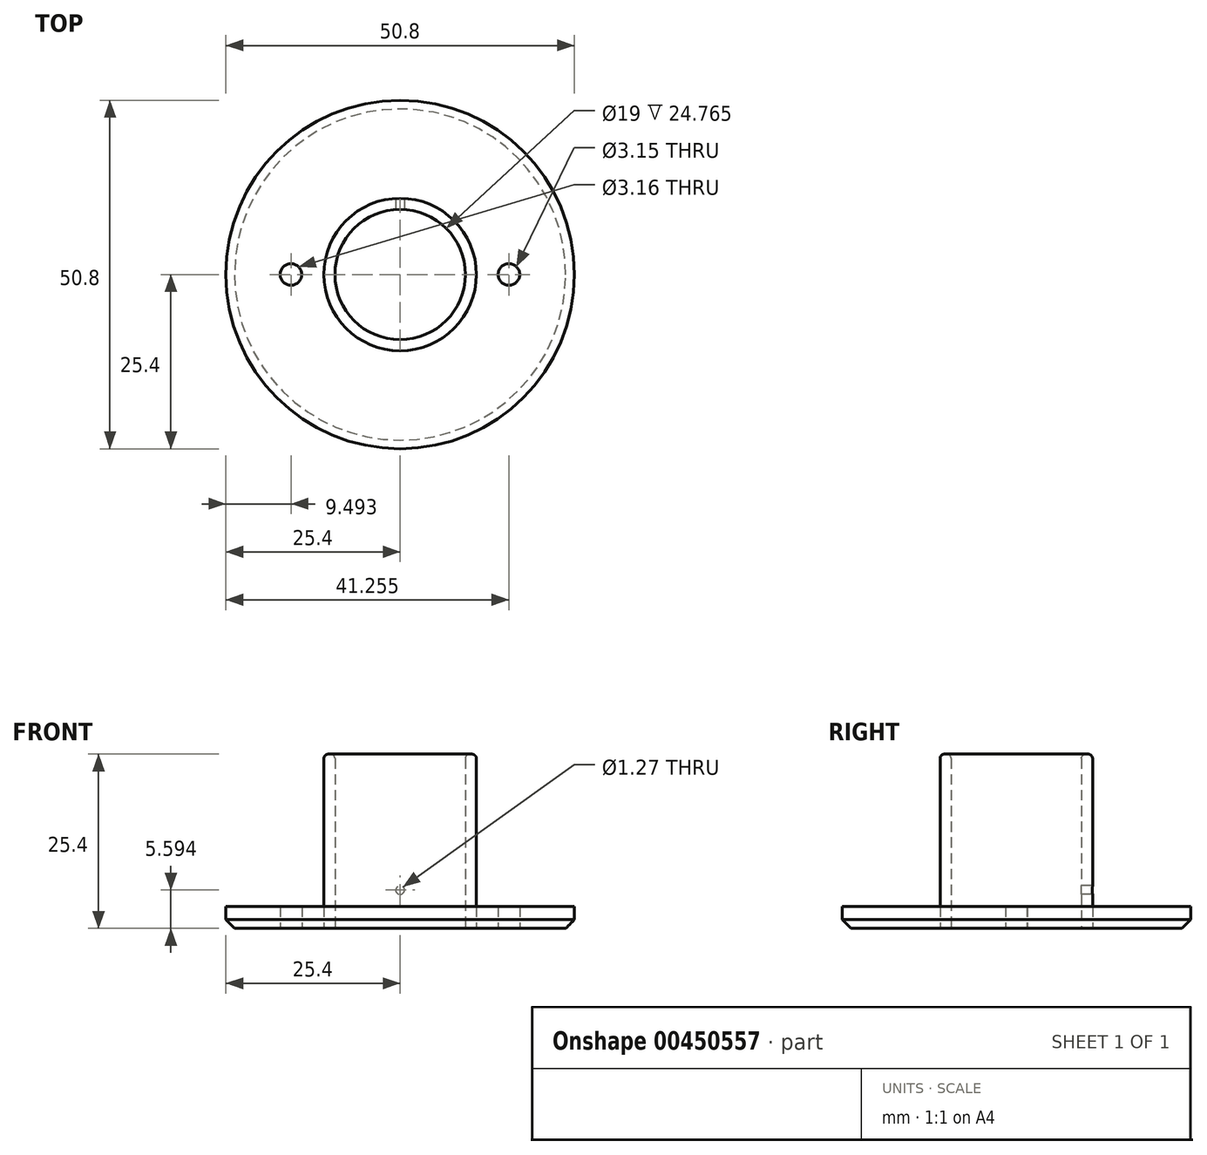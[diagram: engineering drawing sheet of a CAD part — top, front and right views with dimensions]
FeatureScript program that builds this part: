
annotation { "Feature Type Name" : "Feature", "Feature Type Description" : "" }
export const myFeature = defineFeature(function(context is Context, id is Id, definition is map)
    precondition{}
    {
        {
            var Q0;
            Q0=qCreatedBy(makeId("Top.planeOp"),FACE);
            var sketch = newSketch(context, id + "F0", { "sketchPlane" : qUnion([Q0])});
            skCircle(sketch, "E0", {"center": v(0, 0) * mm, "radius": 25.4 * mm});
            skCircle(sketch, "E1", {"center": v(0, 0) * mm, "radius": 9.5 * mm});
            skCircle(sketch, "E2", {"center": v(0, 0) * mm, "radius": 11.1 * mm});
            skLineSegment(sketch, "E3", {"start": v(0, 0) * mm, "end": v(15.86, 0) * mm});
            skLineSegment(sketch, "E4", {"start": v(0, 0) * mm, "end": v(-15.9, 0) * mm});
            skCircle(sketch, "E5", {"center": v(-15.9, 0) * mm, "radius": 1.58 * mm});
            skCircle(sketch, "E6", {"center": v(15.86, 0) * mm, "radius": 1.58 * mm});
            skSolve(sketch);
        }
        {
            var Q0;
            {var subQ0=sQuery(id+"F0.wireOp",EDGE,"E3");var subQ1=sQuery(id+"F0.wireOp",EDGE,"E1");var subQ2=makeQuery(id+"F0.imprint","INTERSECT",VERTEX,{"derivedFrom":[subQ1,subQ0]});Q0=makeQuery(id+"F0.imprint","IMPRINT",FACE,{"disambiguationData":[TD([[makeQuery(id+"F0.imprint","IMPRINT",EDGE,{"disambiguationData":[TD([[subQ2,-1.0]])],"derivedFrom":subQ1}),1.0]])]});}
            var Q1;
            {var subQ0=sQuery(id+"F0.wireOp",EDGE,"E3");var subQ1=sQuery(id+"F0.wireOp",EDGE,"E1");var subQ2=makeQuery(id+"F0.imprint","INTERSECT",VERTEX,{"derivedFrom":[subQ1,subQ0]});Q1=makeQuery(id+"F0.imprint","IMPRINT",FACE,{"disambiguationData":[TD([[makeQuery(id+"F0.imprint","IMPRINT",EDGE,{"disambiguationData":[TD([[subQ2,1.0]])],"derivedFrom":subQ1}),1.0]])]});}
            var Q2;
            {var subQ0=sQuery(id+"F0.wireOp",EDGE,"E3");var subQ1=sQuery(id+"F0.wireOp",EDGE,"E1");var subQ2=makeQuery(id+"F0.imprint","INTERSECT",VERTEX,{"derivedFrom":[subQ1,subQ0]});Q2=makeQuery(id+"F0.imprint","IMPRINT",FACE,{"disambiguationData":[TD([[makeQuery(id+"F0.imprint","IMPRINT",EDGE,{"disambiguationData":[TD([[subQ2,-1.0]])],"derivedFrom":subQ1}),-1.0]])]});}
            var Q3;
            {var subQ0=sQuery(id+"F0.wireOp",EDGE,"E3");var subQ1=sQuery(id+"F0.wireOp",EDGE,"E1");var subQ2=makeQuery(id+"F0.imprint","INTERSECT",VERTEX,{"derivedFrom":[subQ1,subQ0]});Q3=makeQuery(id+"F0.imprint","IMPRINT",FACE,{"disambiguationData":[TD([[makeQuery(id+"F0.imprint","IMPRINT",EDGE,{"disambiguationData":[TD([[subQ2,1.0]])],"derivedFrom":subQ1}),-1.0]])]});}
            var Q4;
            Q4=makeQuery(id+"F0.imprint","IMPRINT",FACE,{"disambiguationData":[TD([[makeQuery(id+"F0.imprint","IMPRINT",EDGE,{"derivedFrom":sQuery(id+"F0.wireOp",EDGE,"E0")}),1.0]])]});
            extrude(context, id + "F1", {"entities" : qUnion([Q0, Q1, Q2, Q3, Q4]), "depth" : 3.17 * mm});
        }
        {
            var Q0;
            {var subQ0=sQuery(id+"F0.wireOp",EDGE,"E3");var subQ1=sQuery(id+"F0.wireOp",EDGE,"E1");var subQ2=makeQuery(id+"F0.imprint","INTERSECT",VERTEX,{"derivedFrom":[subQ1,subQ0]});Q0=makeQuery(id+"F0.imprint","IMPRINT",FACE,{"disambiguationData":[TD([[makeQuery(id+"F0.imprint","IMPRINT",EDGE,{"disambiguationData":[TD([[subQ2,1.0]])],"derivedFrom":subQ1}),-1.0]])]});}
            var Q1;
            {var subQ0=sQuery(id+"F0.wireOp",EDGE,"E3");var subQ1=sQuery(id+"F0.wireOp",EDGE,"E1");var subQ2=makeQuery(id+"F0.imprint","INTERSECT",VERTEX,{"derivedFrom":[subQ1,subQ0]});Q1=makeQuery(id+"F0.imprint","IMPRINT",FACE,{"disambiguationData":[TD([[makeQuery(id+"F0.imprint","IMPRINT",EDGE,{"disambiguationData":[TD([[subQ2,-1.0]])],"derivedFrom":subQ1}),-1.0]])]});}
            var Q2;
            Q2=sQuery(id+"F0.wireOp",EDGE,"E1");
            var Q3;
            Q3=sQuery(id+"F0.wireOp",EDGE,"E2");
            extrude(context, id + "F2", {"entities" : qUnion([Q0, Q1]), "surfaceEntities" : qUnion([Q2, Q3]), "depth" : 25.4 * mm});
        }
        {
            var Q0;
            Q0=qCreatedBy(makeId("Front.planeOp"),FACE);
            var sketch = newSketch(context, id + "F3", { "sketchPlane" : qUnion([Q0])});
            skCircle(sketch, "E7", {"center": v(0, 5.6) * mm, "radius": 0.64 * mm});
            skSolve(sketch);
        }
        {
            var Q0;
            Q0 = qSketchRegion(id + "F3", true);
            extrude(context, id + "F4", {"entities" : qUnion([Q0]), "operationType" : NewBodyOperationType.REMOVE, "oppositeDirection" : true, "depth" : 25.4 * mm});
        }
        {
            var Q0;
            Q0=makeQuery(id+"F1.opExtrude","CAP_EDGE",EDGE,{"disambiguationData":[OSD([sQuery(id+"F0.wireOp",EDGE,"E0")])],"isStart":true});
            chamfer(context, id + "F5", {"entities" : qUnion([Q0]), "width" : 1.27 * mm, "tangentPropagation" : true});
        }
        {
            var Q0;
            Q0=makeQuery(id+"F2.opExtrude","CAP_FACE",FACE,{"disambiguationData":[OSD([sQuery(id+"F0.wireOp",EDGE,"E1"),sQuery(id+"F0.wireOp",EDGE,"E2")])],"isStart":false});
            fillet(context, id + "F6", {"entities" : qUnion([Q0]), "radius" : 0.64 * mm, "tangentPropagation" : true, "allowEdgeOverflow" : false});
        }
    });
